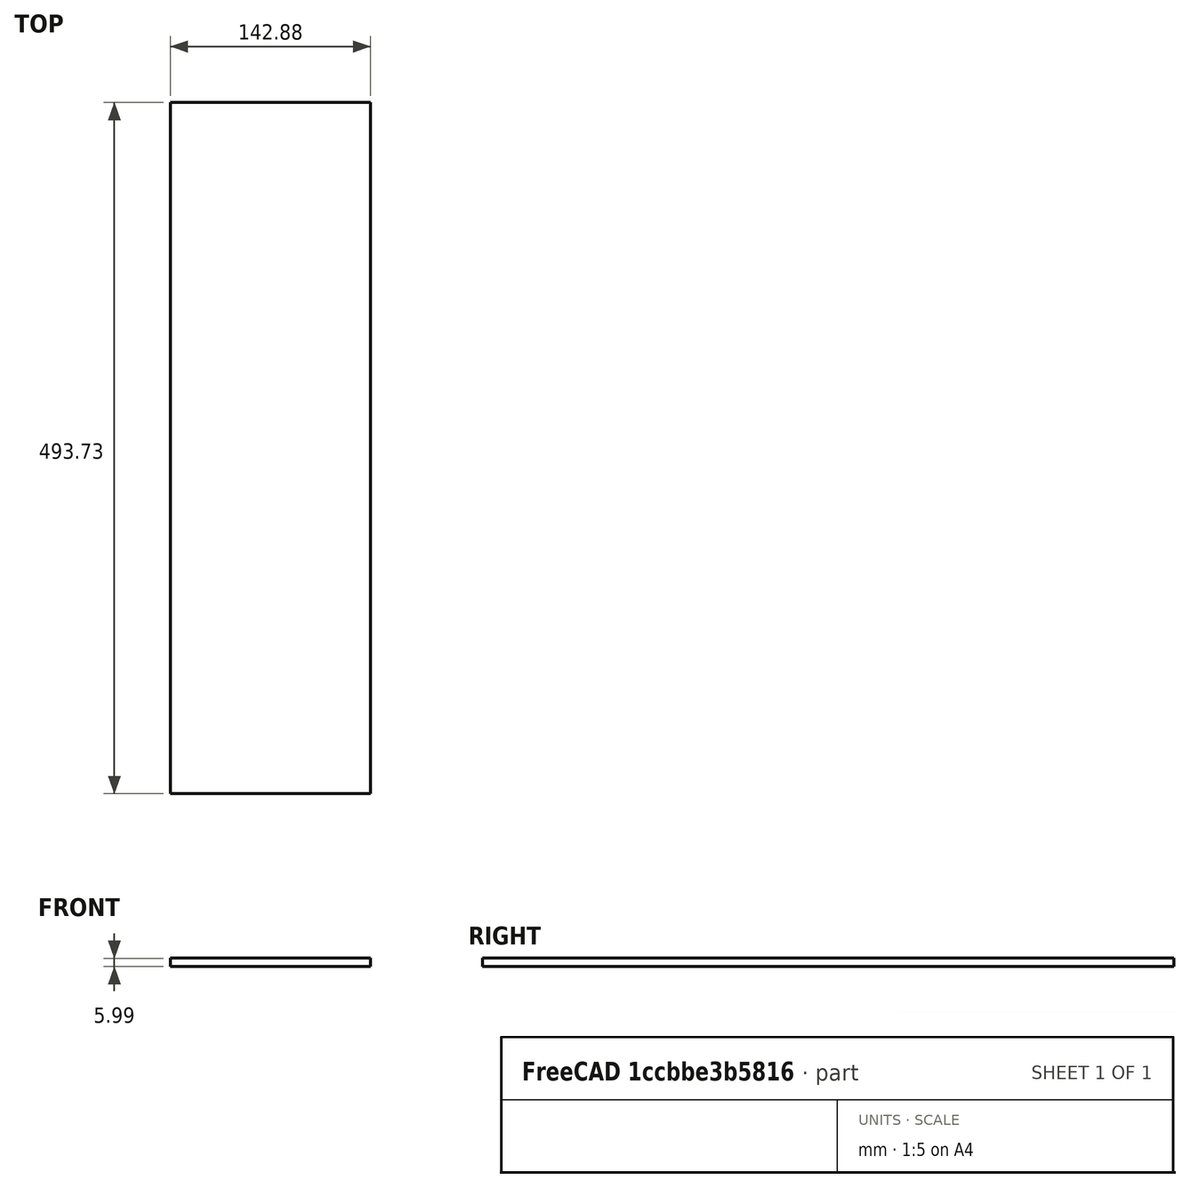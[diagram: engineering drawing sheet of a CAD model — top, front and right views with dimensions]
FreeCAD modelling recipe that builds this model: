
FCSTD DOCUMENT  (FreeCAD 0.19R24267 (Git))
Label: Up1-P5
License: All rights reserved
LicenseURL: http://en.wikipedia.org/wiki/All_rights_reserved
objects: TechDraw::DrawViewDimension×3, TechDraw::DrawProjGroupItem×2, TechDraw::DrawHatch×2, TechDraw::DrawViewAnnotation×2, Sketcher::SketchObject×1, Part::Extrusion×1, TechDraw::DrawSVGTemplate×1, TechDraw::DrawProjGroup×1, TechDraw::DrawPage×1
note: 2 computed .brp shape members not serialized (recipe doc carries the construction recipe); baked Part::Feature solids carry a one-line shape summary decoded from their .brp

FEATURE [Sketcher::SketchObject] Sketch
  FullyConstrained = false
  sketch-geometry (4):
    g0: LineSegment StartX=-30.3473 StartY=0 StartZ=0 EndX=112.528 EndY=0 EndZ=0
    g1: LineSegment StartX=112.528 StartY=0 StartZ=0 EndX=112.528 EndY=493.725 EndZ=0
    g2: LineSegment StartX=112.528 StartY=493.725 StartZ=0 EndX=-30.3473 EndY=493.725 EndZ=0
    g3: LineSegment StartX=-30.3473 StartY=493.725 StartZ=0 EndX=-30.3473 EndY=0 EndZ=0
  constraints (11):
    c: Coincident(g0,g1)
    c: Coincident(g1,g2)
    c: Coincident(g2,g3)
    c: Coincident(g3,g0)
    c: Horizontal(g0)
    c: Horizontal(g2)
    c: Vertical(g1)
    c: Vertical(g3)
    c: PointOnObject(g0,g-1)
    c: DistanceX(g2,g2) = 142.875
    c: DistanceY(g3,g3) = 493.725
FEATURE [Part::Extrusion] Extrude
  Base = -> Sketch
  Dir = (0,0,1)
  DirMode = 2
  FaceMakerClass = Part::FaceMakerBullseye
  LengthFwd = 5.9944
  LengthRev = 0
  Solid = true
  Symmetric = false
FEATURE [TechDraw::DrawSVGTemplate] Template
  Height = 215.9
  Orientation = 1
  Width = 279.4
FEATURE [TechDraw::DrawProjGroupItem] ProjItem  label="Front"
  CoarseView = false
  Direction = (0,0,1)
  Focus = 100
  HardHidden = false
  IsoCount = 0
  IsoHidden = false
  IsoVisible = false
  LockPosition = true
  Perspective = false
  Rotation = 0
  RotationVector = (1,0,0)
  Scale = 0.25
  ScaleType = 2
  SeamHidden = false
  SeamVisible = true
  SmoothHidden = false
  SmoothVisible = true
  Source = -> [Extrude]
  Type = 0
  X = 0
  XDirection = (1,0,0)
  Y = 0
FEATURE [TechDraw::DrawProjGroupItem] ProjItem001  label="Left"
  CoarseView = false
  Direction = (-1,0,1e-16)
  Focus = 100
  HardHidden = false
  IsoCount = 0
  IsoHidden = false
  IsoVisible = false
  LockPosition = false
  Perspective = false
  Rotation = 0
  RotationVector = (1,0,0)
  Scale = 0.25
  ScaleType = 2
  SeamHidden = false
  SeamVisible = true
  SmoothHidden = false
  SmoothVisible = true
  Source = -> [Extrude]
  Type = 1
  X = 53.9046
  XDirection = (1e-16,0,1)
  Y = 0
FEATURE [TechDraw::DrawProjGroup] ProjGroup
  Anchor = -> ProjItem
  AutoDistribute = true
  LockPosition = false
  ProjectionType = 0
  Rotation = 0
  Scale = 0.25
  ScaleType = 2
  Source = -> [Extrude]
  Views = -> [ProjItem,ProjItem001]
  X = 139.7
  Y = 107.95
  spacingX = 15.0114
  spacingY = 15.0114
FEATURE [TechDraw::DrawViewDimension] Dimension
  Arbitrary = false
  ArbitraryTolerances = false
  EqualTolerance = true
  FormatSpec = %.3f
  FormatSpecOverTolerance = %+.3f
  FormatSpecUnderTolerance = %+.3f
  Inverted = false
  LockPosition = false
  MeasureType = 1
  OverTolerance = 0
  References2D = -> [ProjItem]
  Rotation = 0
  ScaleType = 0
  TheoreticalExact = false
  Type = 1
  UnderTolerance = 0
  X = -0.559593
  Y = -70.9489
FEATURE [TechDraw::DrawViewDimension] Dimension001
  Arbitrary = false
  ArbitraryTolerances = false
  EqualTolerance = true
  FormatSpec = %.3f
  FormatSpecOverTolerance = %+.3f
  FormatSpecUnderTolerance = %+.3f
  Inverted = false
  LockPosition = false
  MeasureType = 1
  OverTolerance = 0
  References2D = -> [ProjItem001]
  Rotation = 0
  ScaleType = 0
  TheoreticalExact = false
  Type = 1
  UnderTolerance = 0
  X = 15.0406
  Y = 51.1658
FEATURE [TechDraw::DrawViewDimension] Dimension002
  Arbitrary = false
  ArbitraryTolerances = false
  EqualTolerance = true
  FormatSpec = %.3f
  FormatSpecOverTolerance = %+.3f
  FormatSpecUnderTolerance = %+.3f
  Inverted = false
  LockPosition = false
  MeasureType = 1
  OverTolerance = 0
  References2D = -> [ProjItem]
  Rotation = 0
  ScaleType = 0
  TheoreticalExact = false
  Type = 2
  UnderTolerance = 0
  X = 24.8261
  Y = -1.49331
FEATURE [TechDraw::DrawHatch] Hatch  label="HatchF0"
  HatchPattern = <path>
  Source = -> ProjItem [Face0]
FEATURE [TechDraw::DrawHatch] Hatch001  label="Hatch001F0"
  HatchPattern = <path>
  Source = -> ProjItem001 [Face0]
FEATURE [TechDraw::DrawViewAnnotation] Annotation
  Font = osifont
  LineSpace = 80
  LockPosition = false
  MaxWidth = -1
  Rotation = 0
  ScaleType = 0
  Text = Units: Inches
  TextSize = 5.0038
  TextStyle = 0
  X = 259.08
  Y = 5.08
FEATURE [TechDraw::DrawViewAnnotation] Annotation001
  Font = osifont
  LineSpace = 80
  LockPosition = false
  MaxWidth = -1
  Rotation = 0
  ScaleType = 0
  Text = Figure S3 (Upright) | Panel 5 [back middle] | Quantity: 1
  TextSize = 5.0038
  TextStyle = 0
  X = 32.2145
  Y = 195.58
FEATURE [TechDraw::DrawPage] Page
  KeepUpdated = true
  NextBalloonIndex = 1
  ProjectionType = 0
  Template = -> Template
  Views = -> [ProjGroup,Dimension,Dimension001,Dimension002,Annotation,Annotation001]
note: 2 file-system paths scrubbed to <path> (originals preserved in the JSON sidecar)
